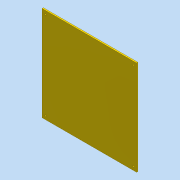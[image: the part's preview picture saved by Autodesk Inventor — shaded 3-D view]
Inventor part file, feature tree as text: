
AUTODESK INVENTOR PART (.ipt)
format: ipt  version: 2016 (Build 200138000, 138)  size: 95,744 bytes
history: native  units: mm
features: hole x4, extrude x1, sketch x1
ambient origin geometry x8: Origin, YZ Plane, XZ Plane, XY Plane, X Axis, Y Axis, Z Axis, Center Point
bodies: Solid1 (feature_tree)
feature tree (6):
  extrude  "Extrusion1"  Depth=220.0mm
  hole  "Hole1"  [1 undecoded]
  hole  "Hole2"  [1 undecoded]
  hole  "Hole3"  [1 undecoded]
  hole  "Hole4"  [1 undecoded]
  sketch  "Sketch1"  dims[d0=220.0mm d1=220.0mm d2=3.0mm d3=0.0mm d4=8.0mm d5=8.0mm d6=3.0mm d7=6.0mm d8=4.0mm d9=2.0mm d10=90.0deg d11=8.0mm d12=20.594885mm d13=8.0mm d14=8.0mm d15=3.0mm d16=6.0mm d17=4.0mm d18=2.0mm d19=90.0deg d20=8.0mm d21=20.594885mm d22=8.0mm d23=8.0mm d24=3.0mm d25=6.0mm d26=4.0mm d27=2.0mm d28=90.0deg d29=8.0mm d30=20.594885mm d31=8.0mm d32=8.0mm d33=3.0mm d34=6.0mm d35=4.0mm d36=2.0mm d37=90.0deg d38=8.0mm d39=20.594885mm]
note: 4 required parameter values undecoded (feature->parameter linkage not recoverable at this tier; creation-order binding heuristic only, values carry confidence <= 0.55)
